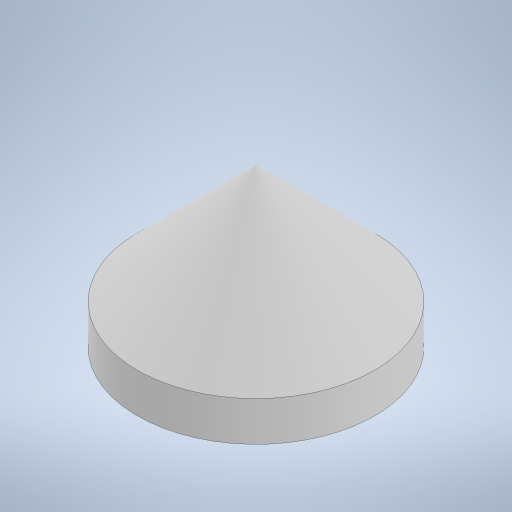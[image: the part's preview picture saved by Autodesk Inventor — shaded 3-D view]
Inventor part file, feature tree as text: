
AUTODESK INVENTOR PART (.ipt)
format: ipt  version: 2023 (Build 270158000, 158)  size: 260,608 bytes
history: native  units: mm
features: extrude x3, sketch x2, chamfer x1
ambient origin geometry x8: Origin, YZ Plane, XZ Plane, XY Plane, X Axis, Y Axis, Z Axis, Center Point
bodies: Solid1 (feature_tree)
feature tree (6):
  sketch  "Sketch1"  dims[d0=28.5mm d1=15.0mm]
  extrude  "Extrusion1"  Depth=15.0mm
  extrude  "Extrusion2"  Depth=2.0mm
  extrude  "Extrusion3"  Depth=6.0mm TaperAngle=0.0deg
  chamfer  "Chamfer1"  Distance=1.0mm
  sketch  "Sketch2"  dims[d2=9.5mm d3=33.0mm d4=6.0mm d5=0.0mm d7=1.0mm d8=40.0mm d10=360.0deg d12=6.0mm d13=0.0mm d14=10.0mm d15=0.0mm d16=16.5mm d17=2.0mm d18=45.0deg]
